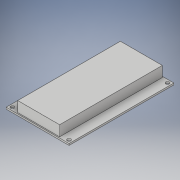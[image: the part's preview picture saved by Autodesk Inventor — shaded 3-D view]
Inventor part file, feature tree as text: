
AUTODESK INVENTOR PART (.ipt)
format: ipt  version: 2019 (Build 230136000, 136)  size: 119,296 bytes
history: native  units: mm
features: sketch x3, extrude x2, hole x1
ambient origin geometry x8: Origin, YZ Plane, XZ Plane, XY Plane, X Axis, Y Axis, Z Axis, Center Point
bodies: Solid1 (feature_tree)
feature tree (6):
  extrude  "Extrusion1"  Depth=100.0mm
  hole  "Hole1"  [1 undecoded]
  extrude  "Extrusion2"  Depth=10.0mm
  sketch  "Sketch1"  dims[d0=60.0mm d1=100.0mm]
  sketch  "Sketch2"  dims[d2=1.6mm d3=0.0mm d4=3.0mm]
  sketch  "Sketch3"  dims[d5=3.0mm d6=20.0mm d8=54.0mm d9=20.0mm d11=94.0mm d14=3.4mm d15=6.0mm d16=6.3mm d17=2.0mm d18=90.0deg d19=8.0mm d20=20.594885mm d21=40.0mm d22=98.0mm d23=10.0mm d24=0.0mm]
note: 1 required parameter value undecoded (feature->parameter linkage not recoverable at this tier; creation-order binding heuristic only, values carry confidence <= 0.55)
